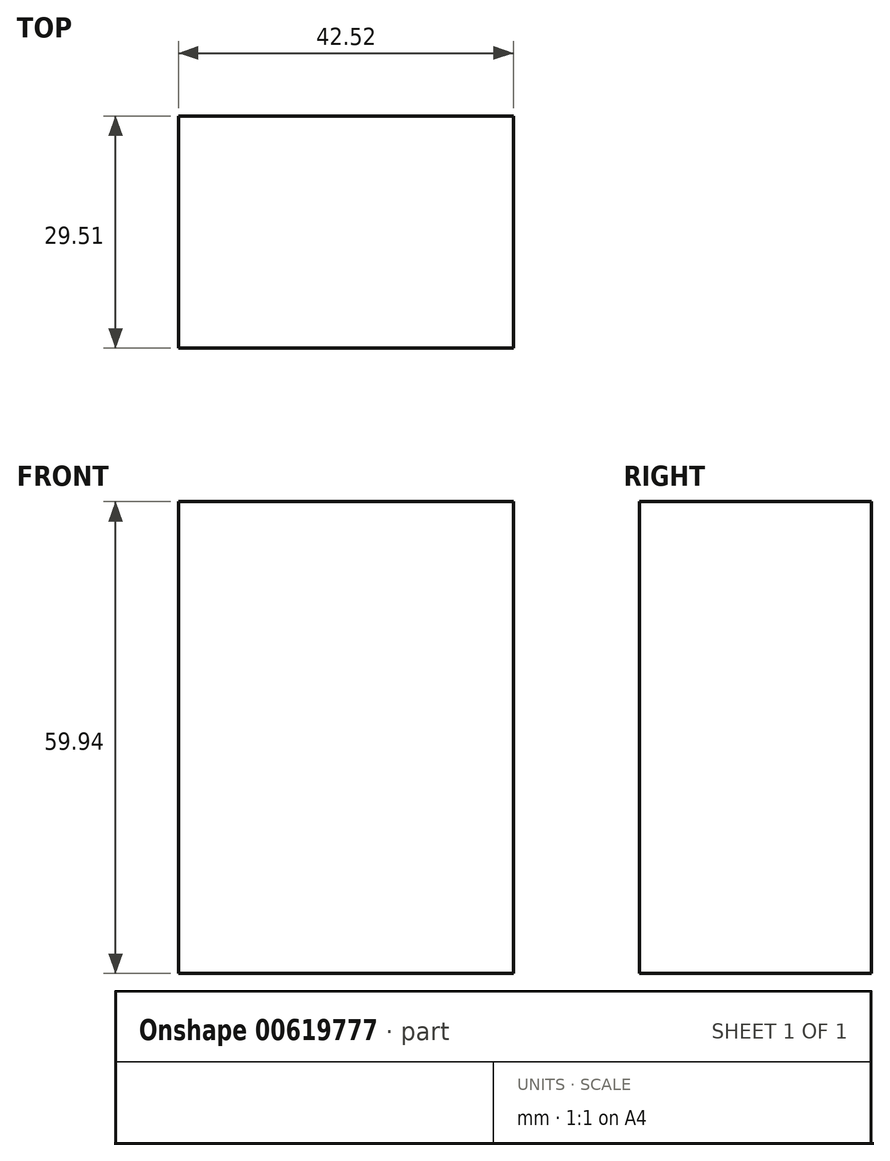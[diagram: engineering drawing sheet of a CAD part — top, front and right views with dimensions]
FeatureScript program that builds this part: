
annotation { "Feature Type Name" : "Feature", "Feature Type Description" : "" }
export const myFeature = defineFeature(function(context is Context, id is Id, definition is map)
    precondition{}
    {
        {
            var Q0;
            Q0=qCreatedBy(makeId("Top.planeOp"),FACE);
            var sketch = newSketch(context, id + "F0", { "sketchPlane" : qUnion([Q0])});
            skLineSegment(sketch, "E0.bottom", {"start": v(0, 0) * mm, "end": v(-42.52, 0) * mm});
            skLineSegment(sketch, "E0.top", {"start": v(0, 29.5) * mm, "end": v(-42.52, 29.5) * mm});
            skLineSegment(sketch, "E0.left", {"start": v(0, 0) * mm, "end": v(0, 29.5) * mm});
            skLineSegment(sketch, "E0.right", {"start": v(-42.52, 0) * mm, "end": v(-42.52, 29.5) * mm});
            skSolve(sketch);
        }
        {
            var Q0;
            Q0=makeQuery(id+"F0.imprint","IMPRINT",FACE,{"disambiguationData":[TD([[makeQuery(id+"F0.imprint","IMPRINT",EDGE,{"derivedFrom":sQuery(id+"F0.wireOp",EDGE,"E0.bottom")}),-1.0]])]});
            extrude(context, id + "F1", {"entities" : qUnion([Q0]), "oppositeDirection" : true, "depth" : 59.94 * mm, "offsetDistance" : 25.4 * mm});
        }
    });
